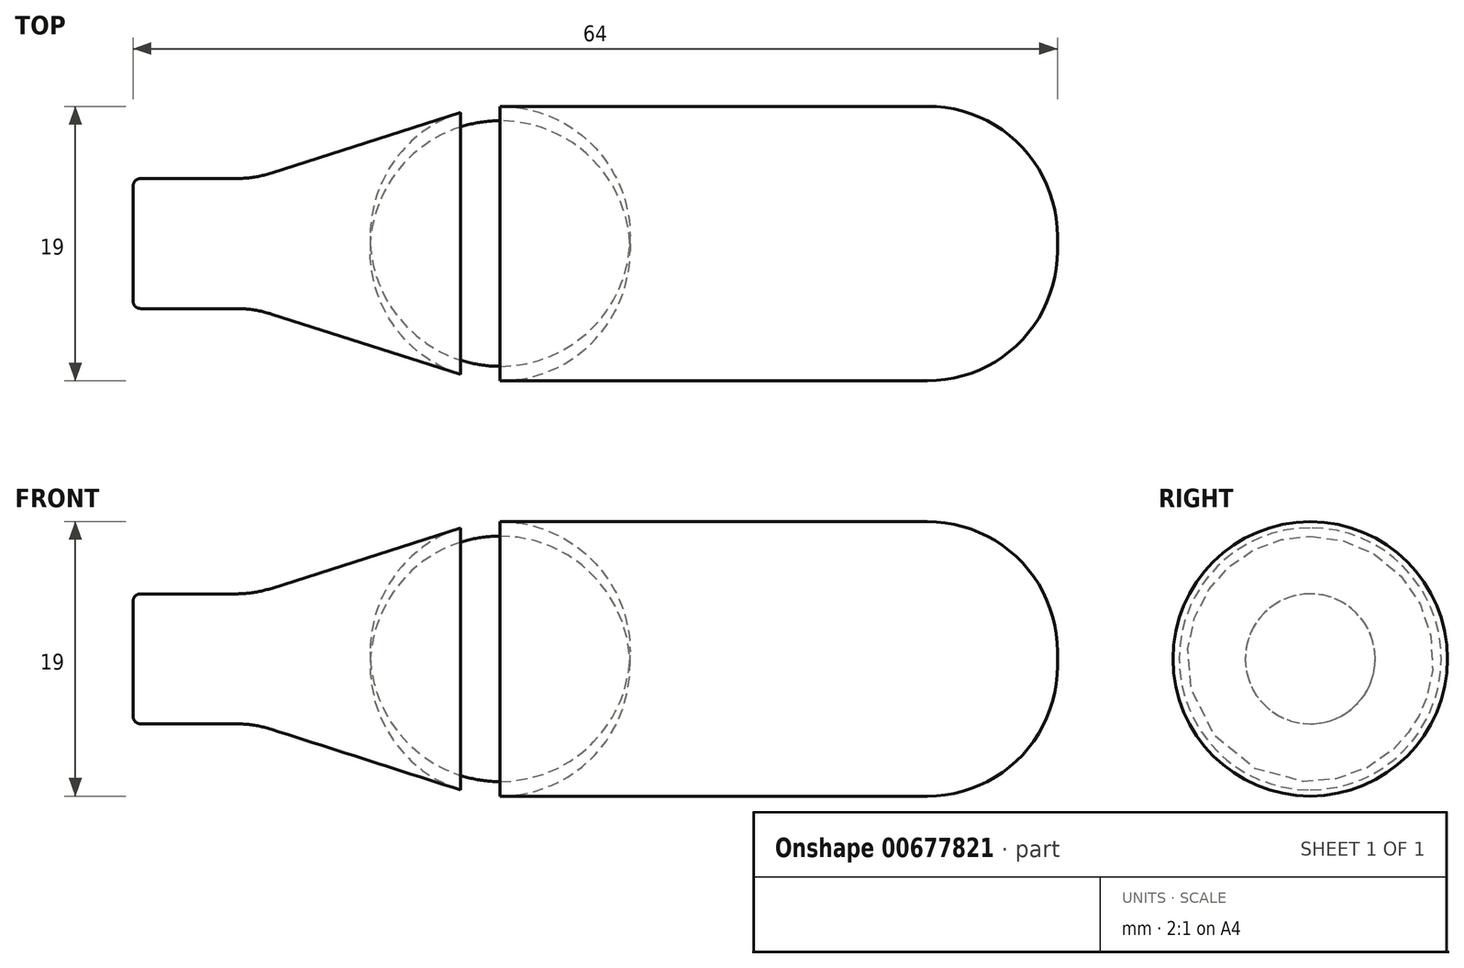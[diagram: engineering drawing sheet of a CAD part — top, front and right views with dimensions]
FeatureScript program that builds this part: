
annotation { "Feature Type Name" : "Feature", "Feature Type Description" : "" }
export const myFeature = defineFeature(function(context is Context, id is Id, definition is map)
    precondition{}
    {
        {
            var Q0;
            Q0=qCreatedBy(makeId("Front.planeOp"),FACE);
            var sketch = newSketch(context, id + "F0", { "sketchPlane" : qUnion([Q0])});
            skLineSegment(sketch, "E0", {"start": v(0, 0) * mm, "end": v(64, 0) * mm});
            skLineSegment(sketch, "E1", {"start": v(64, 9.5) * mm, "end": v(24, 9.5) * mm});
            skLineSegment(sketch, "E2", {"start": v(24, 9.5) * mm, "end": v(8.38, 4.5) * mm});
            skLineSegment(sketch, "E3", {"start": v(8.38, 4.5) * mm, "end": v(0, 4.5) * mm});
            skLineSegment(sketch, "E4", {"start": v(0, 4.5) * mm, "end": v(0, 0) * mm});
            skLineSegment(sketch, "E5", {"start": v(64, 9.5) * mm, "end": v(64, 0) * mm});
            skSolve(sketch);
        }
        {
            var Q0;
            Q0=makeQuery(id+"F0.imprint","IMPRINT",FACE,{"disambiguationData":[TD([[makeQuery(id+"F0.imprint","IMPRINT",EDGE,{"derivedFrom":sQuery(id+"F0.wireOp",EDGE,"E0")}),1.0]])]});
            var Q1;
            Q1=sQuery(id+"F0.wireOp",EDGE,"E0");
            revolve(context, id + "F1", {"entities" : qUnion([Q0]), "axis" : qUnion([Q1]), "revolveType" : RevolveType.FULL});
        }
        {
            var Q0;
            Q0=makeQuery(id+"F1.opRevolve","SWEPT_EDGE",EDGE,{"disambiguationData":[OSD([sQuery(id+"F0.wireOp",EDGE,"E1"),sQuery(id+"F0.wireOp",EDGE,"E5")])]});
            fillet(context, id + "F2", {"entities" : qUnion([Q0]), "radius" : 9 * mm, "tangentPropagation" : true, "allowEdgeOverflow" : false});
        }
        {
            var Q0;
            Q0=makeQuery(id+"F1.opRevolve","SWEPT_EDGE",EDGE,{"disambiguationData":[OSD([sQuery(id+"F0.wireOp",EDGE,"E1"),sQuery(id+"F0.wireOp",EDGE,"E2")])]});
            fillet(context, id + "F3", {"entities" : qUnion([Q0]), "radius" : 9 * mm, "tangentPropagation" : true, "allowEdgeOverflow" : false});
        }
        {
            var Q0;
            Q0=makeQuery(id+"F1.opRevolve","SWEPT_EDGE",EDGE,{"disambiguationData":[OSD([sQuery(id+"F0.wireOp",EDGE,"E2"),sQuery(id+"F0.wireOp",EDGE,"E3")])]});
            fillet(context, id + "F4", {"entities" : qUnion([Q0]), "radius" : 8 * mm, "tangentPropagation" : true, "allowEdgeOverflow" : false});
        }
        {
            var Q0;
            Q0=makeQuery(id+"F1.opRevolve","SWEPT_EDGE",EDGE,{"disambiguationData":[OSD([sQuery(id+"F0.wireOp",EDGE,"E3"),sQuery(id+"F0.wireOp",EDGE,"E4")])]});
            fillet(context, id + "F5", {"entities" : qUnion([Q0]), "radius" : .5 * mm, "tangentPropagation" : true, "allowEdgeOverflow" : false});
        }
    });
